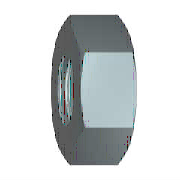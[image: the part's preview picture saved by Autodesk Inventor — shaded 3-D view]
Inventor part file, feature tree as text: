
AUTODESK INVENTOR PART (.ipt)
format: ipt  version: 2019 (Build 230136000, 136)  size: 161,792 bytes
history: native  units: mm (DEFAULTED — no unit token found)
features: sketch x3, chamfer x1, hole x1, other x1, plane x1
ambient origin geometry x7: Origin, YZ Plane, XZ Plane, X Axis, Y Axis, Z Axis, Center Point
bodies: Solid1 (feature_tree), Body (feature_tree)
feature tree (7):
  chamfer  "Chamfer1"  Angle=30.0deg  [1 undecoded]
  hole  "Thread"  [1 undecoded]
  other  "Work Axis1"
  plane  "Work Plane1"
  sketch  "Sketch1"  dims[d0=6.350853mm]
  sketch  "Sketch2"  dims[d1=2.4mm]
  sketch  "Sketch3"  dims[d2=0.0mm d3=30.0deg d4=30.0deg d5=4.5mm d6=4.5mm d7=90.0deg d25=2.459mm d26=6.0mm d27=4.0mm d28=2.0mm d29=14.3117mm d30=8.0mm d31=20.594885mm d8=0.270633mm d9=30.0deg d10=0.270633mm d11=30.0deg d13=0.0mm d14=0.0mm d39=0.0mm d40=0.270633mm d41=0.270633mm d42=0.0mm]
note: 2 required parameter values undecoded (feature->parameter linkage not recoverable at this tier; creation-order binding heuristic only, values carry confidence <= 0.55)
